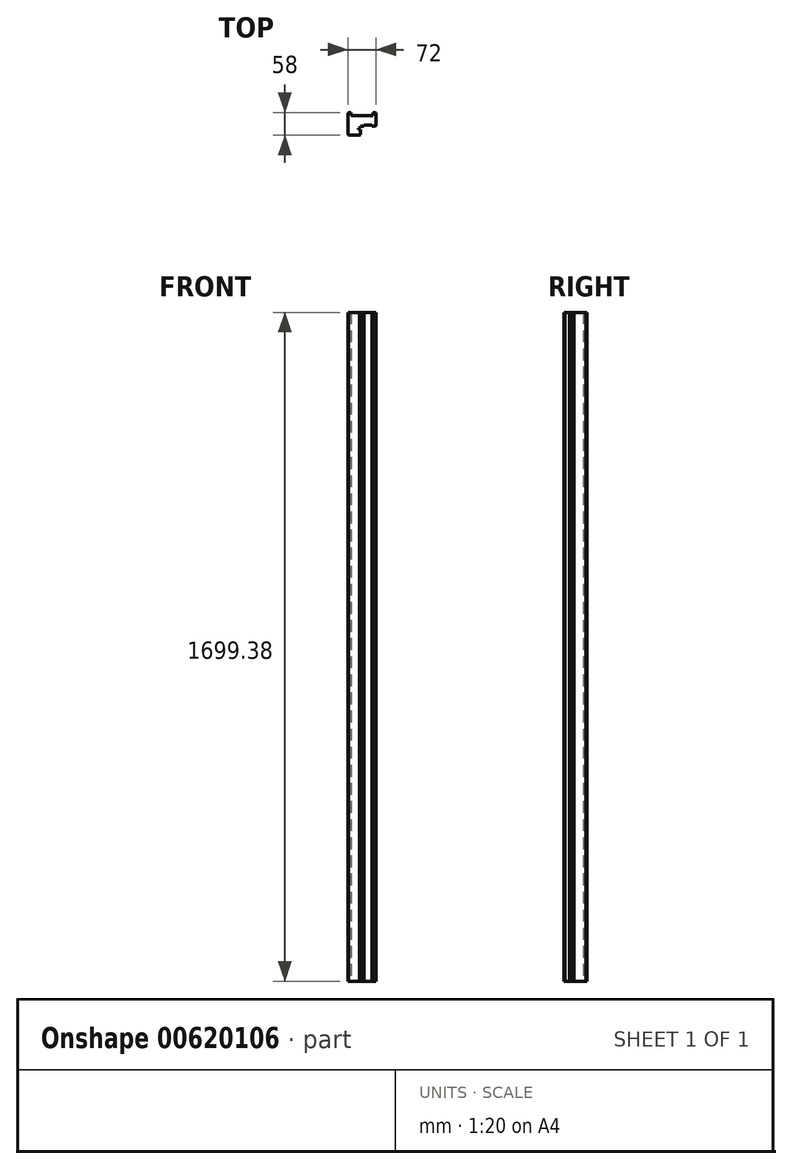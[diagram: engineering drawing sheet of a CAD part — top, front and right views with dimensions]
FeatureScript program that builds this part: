
annotation { "Feature Type Name" : "Feature", "Feature Type Description" : "" }
export const myFeature = defineFeature(function(context is Context, id is Id, definition is map)
    precondition{}
    {
        {
            var Q0;
            Q0=qCreatedBy(makeId("Top.planeOp"),FACE);
            var sketch = newSketch(context, id + "F0", { "sketchPlane" : qUnion([Q0])});
            skLineSegment(sketch, "E0.bottom", {"start": v(-4.28, -28.86) * mm, "end": v(-36.28, -28.86) * mm});
            skLineSegment(sketch, "E0.top", {"start": v(35.72, 29.14) * mm, "end": v(27.22, 29.14) * mm});
            skLineSegment(sketch, "E0.left", {"start": v(35.72, -5.86) * mm, "end": v(35.72, 29.14) * mm});
            skLineSegment(sketch, "E0.right", {"start": v(-36.28, -28.86) * mm, "end": v(-36.28, 29.14) * mm});
            skPoint(sketch, "E0.middle", {"position": v(-0.28, 0.14) * mm});
            skLineSegment(sketch, "E1.top", {"start": v(-27.78, 20.64) * mm, "end": v(27.22, 20.64) * mm});
            skLineSegment(sketch, "E1.left", {"start": v(-27.78, 29.14) * mm, "end": v(-27.78, 20.64) * mm});
            skLineSegment(sketch, "E1.right", {"start": v(27.22, 29.14) * mm, "end": v(27.22, 20.64) * mm});
            skLineSegment(sketch, "E2.trimOffspring", {"start": v(-27.78, 29.14) * mm, "end": v(-36.28, 29.14) * mm});
            skLineSegment(sketch, "E3.top", {"start": v(35.72, -5.86) * mm, "end": v(24.72, -5.86) * mm});
            skLineSegment(sketch, "E3.right", {"start": v(-4.28, -28.86) * mm, "end": v(-4.28, -14.64) * mm});
            skLineSegment(sketch, "E4.top", {"start": v(4.72, -3.36) * mm, "end": v(24.72, -3.36) * mm});
            skLineSegment(sketch, "E4.left", {"start": v(4.72, -5.86) * mm, "end": v(4.72, -3.36) * mm});
            skLineSegment(sketch, "E5.trimOffspring", {"start": v(4.72, -5.86) * mm, "end": v(-4.28, -5.86) * mm});
            skLineSegment(sketch, "E6", {"start": v(24.72, -3.36) * mm, "end": v(24.72, -5.86) * mm});
            skLineSegment(sketch, "E7.bottom", {"start": v(-4.28, -14.64) * mm, "end": v(-9.28, -14.64) * mm});
            skLineSegment(sketch, "E7.top", {"start": v(-4.28, -10.64) * mm, "end": v(-9.28, -10.64) * mm});
            skLineSegment(sketch, "E7.right", {"start": v(-9.28, -14.64) * mm, "end": v(-9.28, -10.64) * mm});
            skLineSegment(sketch, "E8.trimOffspring", {"start": v(-4.28, -10.64) * mm, "end": v(-4.28, -5.86) * mm});
            skSolve(sketch);
        }
        {
            var Q0;
            Q0=makeQuery(id+"F0.imprint","IMPRINT",FACE,{"disambiguationData":[TD([[makeQuery(id+"F0.imprint","IMPRINT",EDGE,{"derivedFrom":sQuery(id+"F0.wireOp",EDGE,"E0.bottom")}),-1.0]])]});
            extrude(context, id + "F1", {"entities" : qUnion([Q0]), "depth" : 1699.38 * mm, "offsetDistance" : 25 * mm});
        }
        {
            var Q0;
            Q0=makeQuery(id+"F1.opExtrude","SWEPT_EDGE",EDGE,{"disambiguationData":[OSD([sQuery(id+"F0.wireOp",EDGE,"E0.bottom"),sQuery(id+"F0.wireOp",EDGE,"E0.right")])]});
            var Q1;
            Q1=makeQuery(id+"F1.opExtrude","SWEPT_EDGE",EDGE,{"disambiguationData":[OSD([sQuery(id+"F0.wireOp",EDGE,"E0.right"),sQuery(id+"F0.wireOp",EDGE,"E2.trimOffspring")])]});
            var Q2;
            Q2=makeQuery(id+"F1.opExtrude","SWEPT_EDGE",EDGE,{"disambiguationData":[OSD([sQuery(id+"F0.wireOp",EDGE,"E0.bottom"),sQuery(id+"F0.wireOp",EDGE,"E3.right")])]});
            var Q3;
            Q3=makeQuery(id+"F1.opExtrude","SWEPT_EDGE",EDGE,{"disambiguationData":[OSD([sQuery(id+"F0.wireOp",EDGE,"E0.left"),sQuery(id+"F0.wireOp",EDGE,"E3.top")])]});
            var Q4;
            Q4=makeQuery(id+"F1.opExtrude","SWEPT_EDGE",EDGE,{"disambiguationData":[OSD([sQuery(id+"F0.wireOp",EDGE,"E0.top"),sQuery(id+"F0.wireOp",EDGE,"E0.left")])]});
            chamfer(context, id + "F2", {"entities" : qUnion([Q0, Q1, Q2, Q3, Q4]), "width" : 2 * mm, "tangentPropagation" : true});
        }
    });
